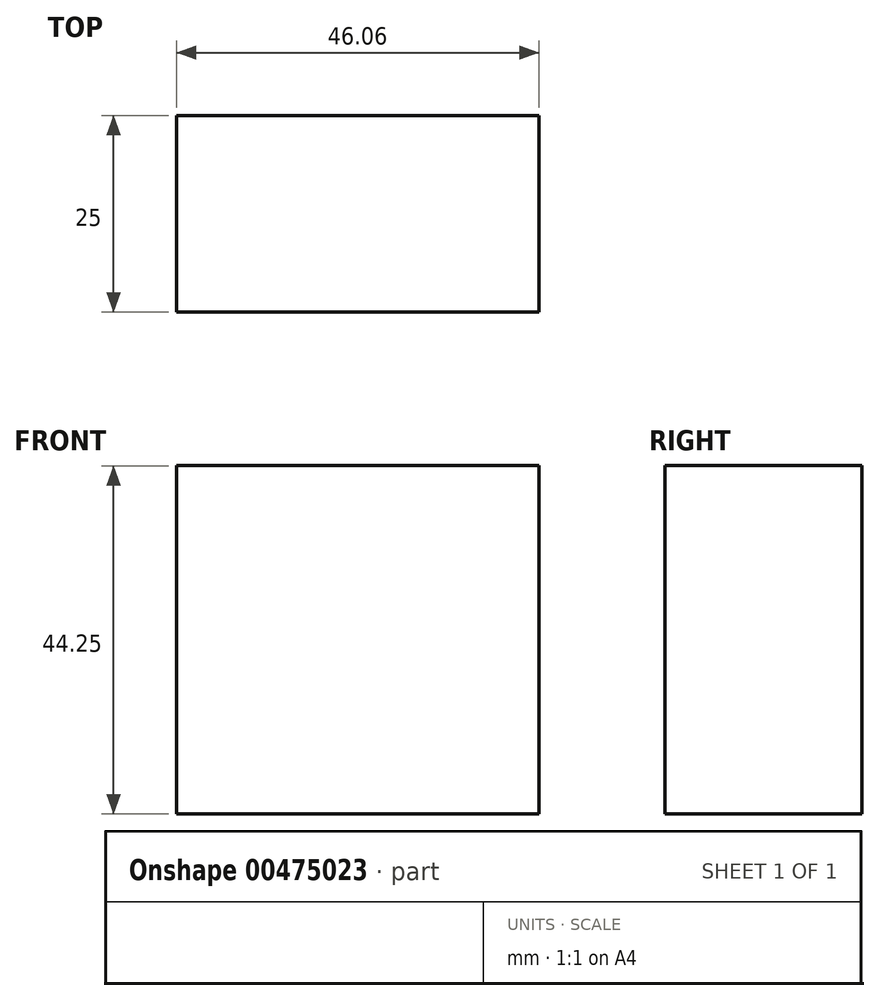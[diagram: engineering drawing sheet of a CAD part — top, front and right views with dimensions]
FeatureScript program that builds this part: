
annotation { "Feature Type Name" : "Feature", "Feature Type Description" : "" }
export const myFeature = defineFeature(function(context is Context, id is Id, definition is map)
    precondition{}
    {
        {
            var Q0;
            Q0=qCreatedBy(makeId("Front.planeOp"),FACE);
            var sketch = newSketch(context, id + "F0", { "sketchPlane" : qUnion([Q0])});
            skLineSegment(sketch, "E0.bottom", {"start": v(-87.45, 0) * mm, "end": v(-41.39, 0) * mm});
            skLineSegment(sketch, "E0.top", {"start": v(-87.45, 44.25) * mm, "end": v(-41.39, 44.25) * mm});
            skLineSegment(sketch, "E0.left", {"start": v(-87.45, 0) * mm, "end": v(-87.45, 44.25) * mm});
            skLineSegment(sketch, "E0.right", {"start": v(-41.39, 0) * mm, "end": v(-41.39, 44.25) * mm});
            skPoint(sketch, "E0.middle", {"position": v(-64.42, 22.13) * mm});
            skSolve(sketch);
        }
        {
            var Q0;
            Q0=makeQuery(id+"F0.imprint","IMPRINT",FACE,{"disambiguationData":[TD([[makeQuery(id+"F0.imprint","IMPRINT",EDGE,{"derivedFrom":sQuery(id+"F0.wireOp",EDGE,"E0.bottom")}),1.0]])]});
            extrude(context, id + "F1", {"entities" : qUnion([Q0]), "depth" : 25 * mm});
        }
    });
